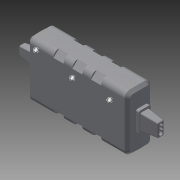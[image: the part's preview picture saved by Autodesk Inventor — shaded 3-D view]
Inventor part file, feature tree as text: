
AUTODESK INVENTOR PART (.ipt)
format: ipt  version: 2014 SP1 (Build 180222100, 222)  size: 820,224 bytes
history: native  units: in
note: dims shown in document units (in); Inventor stores cm internally (conversion verified against a paired STEP export)
features: imported_body x6, other x6, sketch x1
ambient origin geometry x8: Origin, YZ Plane, XZ Plane, XY Plane, X Axis, Y Axis, Z Axis, Center Point
bodies: Body1 (feature_tree), Body2 (feature_tree), Body3 (feature_tree), Body4 (feature_tree), Body5 (feature_tree)
feature tree (13):
  imported_body  "Imported1"
  other  "Motor Controller"
  sketch  "Sketch1"  dims[d0=0.5in d3=0.0in d4=0.0in d5=0.0in]
  other  "left axis"
  other  "right axis"
  other  "Imported1_1"
  other  "Imported1_2"
  other  "Imported1_3"
  imported_body  "Base1"
  imported_body  "Base2"
  imported_body  "Base3"
  imported_body  "Base4"
  imported_body  "Base5"
